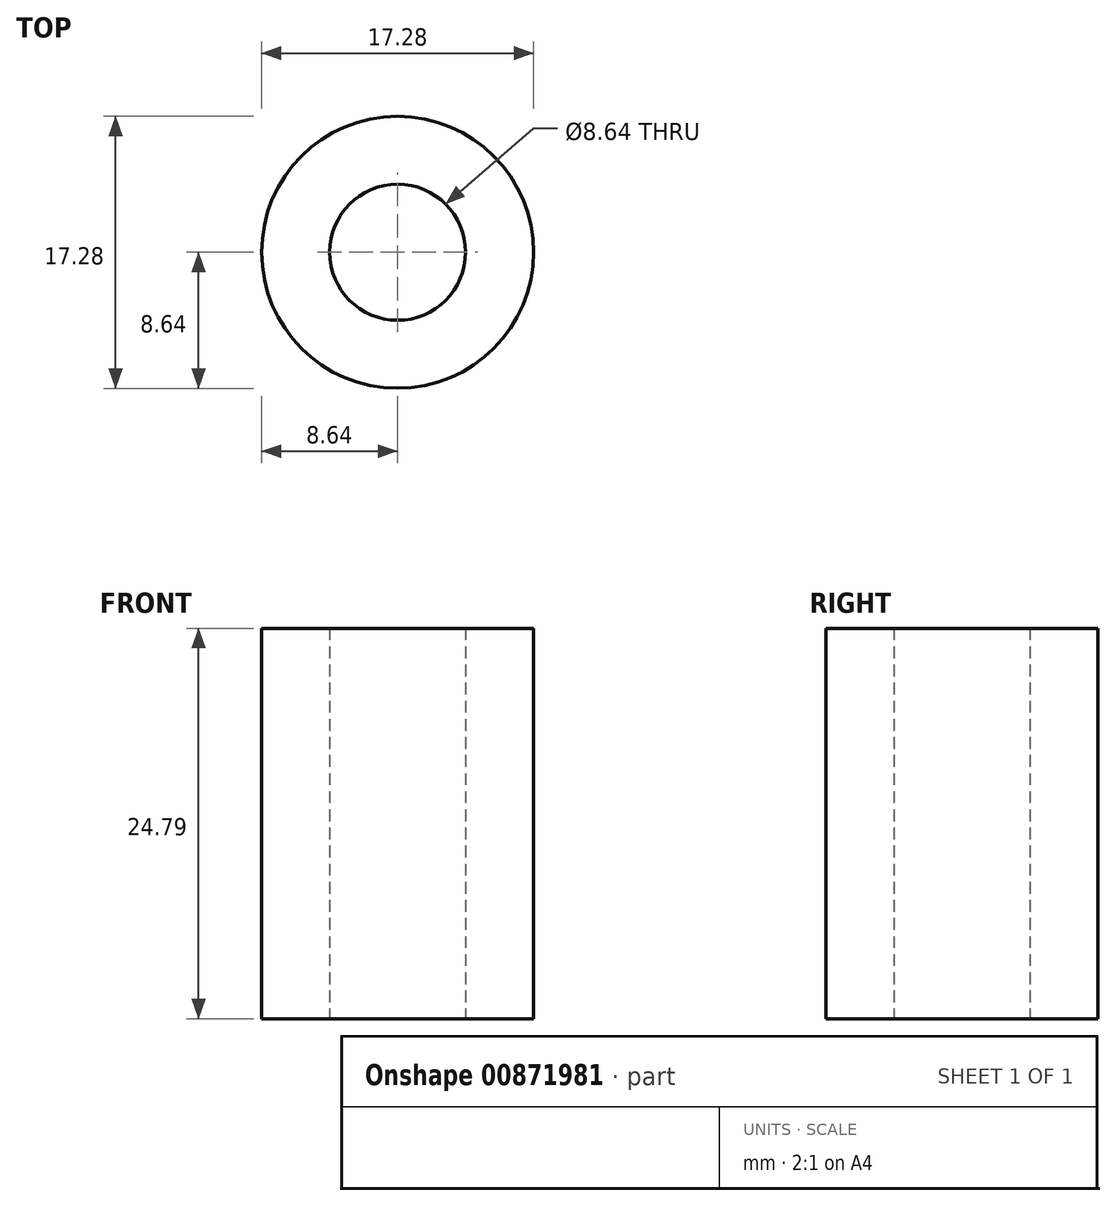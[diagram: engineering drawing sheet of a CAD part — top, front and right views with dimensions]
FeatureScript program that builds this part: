
annotation { "Feature Type Name" : "Feature", "Feature Type Description" : "" }
export const myFeature = defineFeature(function(context is Context, id is Id, definition is map)
    precondition{}
    {
        {
            var Q0;
            Q0=qCreatedBy(makeId("Front.planeOp"),FACE);
            var sketch = newSketch(context, id + "F0", { "sketchPlane" : qUnion([Q0])});
            skLineSegment(sketch, "E0", {"start": v(0, 0) * mm, "end": v(0, 24.8) * mm, "construction": true});
            skLineSegment(sketch, "E1", {"start": v(4.32, 0) * mm, "end": v(8.64, 0) * mm});
            skLineSegment(sketch, "E2", {"start": v(8.64, 0) * mm, "end": v(8.64, 24.8) * mm});
            skLineSegment(sketch, "E3", {"start": v(8.64, 24.8) * mm, "end": v(4.32, 24.8) * mm});
            skLineSegment(sketch, "E4", {"start": v(4.32, 24.8) * mm, "end": v(4.32, 0) * mm});
            skSolve(sketch);
        }
        {
            var Q0;
            Q0 = qSketchRegion(id + "F0", true);
            var Q1;
            Q1=sQuery(id+"F0.wireOp",EDGE,"E0");
            revolve(context, id + "F1", {"surfaceOperationType" : NewSurfaceOperationType.NEW, "entities" : qUnion([Q0]), "axis" : qUnion([Q1]), "revolveType" : RevolveType.FULL});
        }
    });
